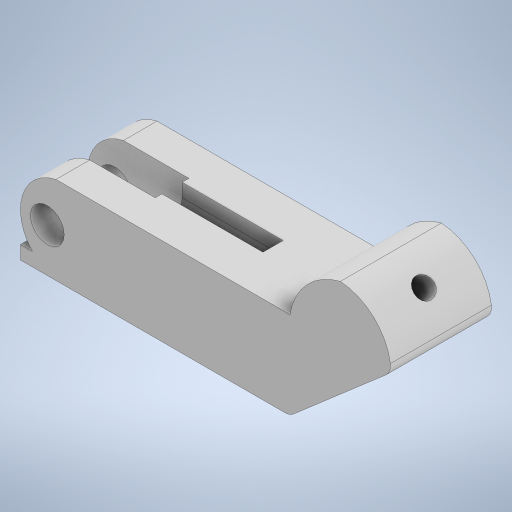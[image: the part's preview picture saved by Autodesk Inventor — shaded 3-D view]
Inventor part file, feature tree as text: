
AUTODESK INVENTOR PART (.ipt)
format: ipt  version: 2023 (Build 270158000, 158)  size: 317,440 bytes
history: native  units: in
note: dims shown in document units (in); Inventor stores cm internally (conversion verified against a paired STEP export)
features: extrude x5, sketch x4, plane x2, loft x1, other x1
ambient origin geometry x8: Origin, YZ Plane, XZ Plane, XY Plane, X Axis, Y Axis, Z Axis, Center Point
bodies: Solid1 (feature_tree)
feature tree (13):
  extrude  "Extrusion1"  Depth=0.315in
  plane  "Work Plane1"
  sketch  "Sketch2"  dims[d3=0.1969in d4=0.5906in]
  extrude  "Extrusion2"  Depth=0.5906in
  sketch  "Sketch3"  dims[d5=0.5118in d7=0.3937in]
  extrude  "Extrusion3"  Depth=0.3937in
  extrude  "Extrusion4"  Depth=0.0787in
  extrude  "Extrusion5"  Depth=0.0787in
  plane  "Work Plane2"
  loft  "Loft1"
  sketch  "Sketch1"  dims[d0=1.5748in d2=0.315in]
  sketch  "Sketch4"  dims[d8=0.315in d9=0.0787in d10=0.0787in d11=0.3937in d12=0.5906in d13=0.0in d14=0.3937in d15=0.0984in d16=0.0984in d17=0.5906in d18=0.5906in d19=0.0591in d20=0.0591in d21=0.5906in d22=0.0in d23=0.0in d25=0.1181in d27=0.1181in d28=0.0in d29=0.0in d30=1.0236in d31=0.0in d32=0.4724in d33=0.0in d34=0.1181in d35=0.0in d36=90.0deg d37=0.0in d38=90.0deg]
  other  "Edges1"
